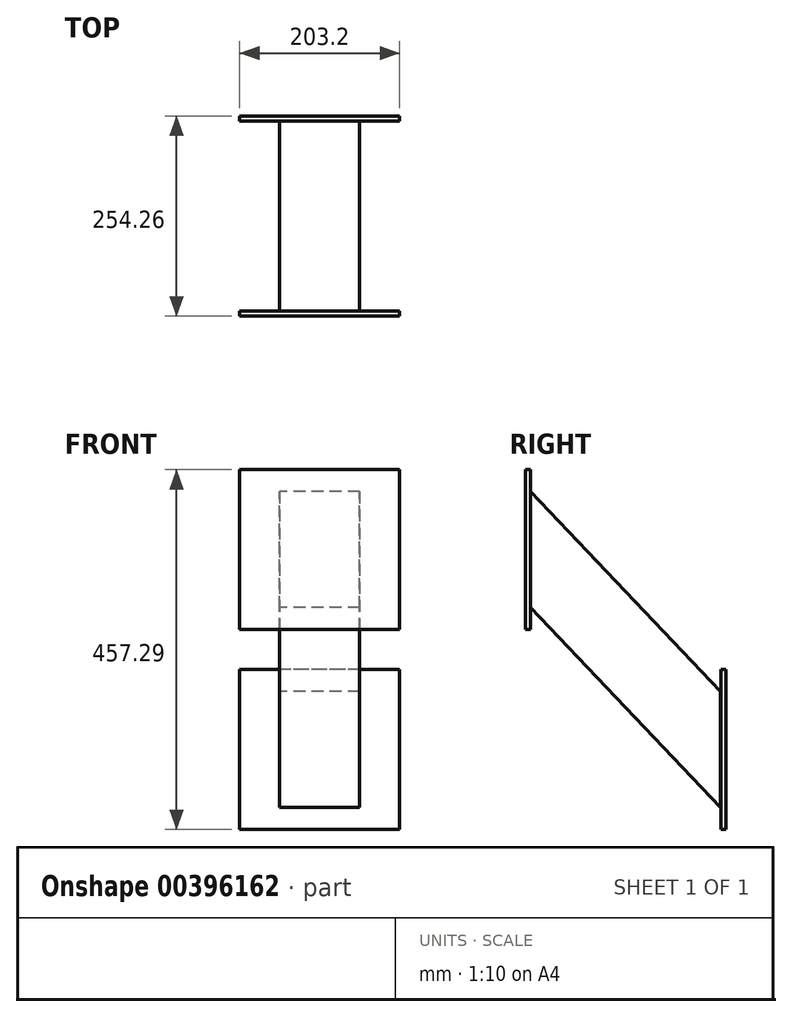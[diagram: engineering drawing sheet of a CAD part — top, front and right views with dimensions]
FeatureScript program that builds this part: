
annotation { "Feature Type Name" : "Feature", "Feature Type Description" : "" }
export const myFeature = defineFeature(function(context is Context, id is Id, definition is map)
    precondition{}
    {
        {
            var Q0;
            Q0=qCreatedBy(makeId("Right.planeOp"),FACE);
            var sketch = newSketch(context, id + "F0", { "sketchPlane" : qUnion([Q0])});
            skLineSegment(sketch, "E0.bottom", {"start": v(-67, -16.54) * mm, "end": v(-73.36, -16.54) * mm});
            skLineSegment(sketch, "E0.top", {"start": v(-67, 186.66) * mm, "end": v(-73.36, 186.66) * mm});
            skLineSegment(sketch, "E0.left", {"start": v(-67, -16.54) * mm, "end": v(-67, 186.66) * mm});
            skLineSegment(sketch, "E0.right", {"start": v(-73.36, -16.54) * mm, "end": v(-73.36, 186.66) * mm});
            skPoint(sketch, "E0.middle", {"position": v(-70.18, 85.06) * mm});
            skLineSegment(sketch, "E1", {"start": v(-67, 158.75) * mm, "end": v(174.3, -95.25) * mm});
            skLineSegment(sketch, "E2", {"start": v(174.3, -95.25) * mm, "end": v(174.3, -242.77) * mm});
            skLineSegment(sketch, "E3", {"start": v(174.3, -242.77) * mm, "end": v(-67, 11.23) * mm});
            skLineSegment(sketch, "E4", {"start": v(-67, 11.23) * mm, "end": v(-67, 158.75) * mm});
            skLineSegment(sketch, "E5.bottom", {"start": v(174.55, -67.39) * mm, "end": v(180.9, -67.39) * mm});
            skLineSegment(sketch, "E5.top", {"start": v(174.55, -270.63) * mm, "end": v(180.9, -270.63) * mm});
            skLineSegment(sketch, "E5.left", {"start": v(174.55, -67.39) * mm, "end": v(174.55, -270.63) * mm});
            skLineSegment(sketch, "E5.right", {"start": v(180.9, -67.39) * mm, "end": v(180.9, -270.63) * mm});
            skSolve(sketch);
        }
        {
            var Q0;
            {var subQ3=sQuery(id+"F0.wireOp",EDGE,"E0.bottom");Q0=makeQuery(id+"F0.imprint","IMPRINT",FACE,{"disambiguationData":[TD([[makeQuery(id+"F0.imprint","IMPRINT",EDGE,{"derivedFrom":subQ3}),-1.0]])]});}
            extrude(context, id + "F1", {"entities" : qUnion([Q0]), "depth" : 101.6 * mm, "hasSecondDirection" : true, "secondDirectionOppositeDirection" : true, "secondDirectionDepth" : 101.6 * mm});
        }
        {
            var Q0;
            Q0=makeQuery(id+"F0.imprint","IMPRINT",FACE,{"disambiguationData":[TD([[makeQuery(id+"F0.imprint","IMPRINT",EDGE,{"derivedFrom":sQuery(id+"F0.wireOp",EDGE,"E1")}),-1.0]])]});
            extrude(context, id + "F2", {"entities" : qUnion([Q0]), "operationType" : NewBodyOperationType.ADD, "depth" : 50.8 * mm, "hasSecondDirection" : true, "secondDirectionOppositeDirection" : true, "secondDirectionDepth" : 50.8 * mm});
        }
        {
            var Q0;
            Q0=makeQuery(id+"F0.imprint","IMPRINT",FACE,{"disambiguationData":[TD([[makeQuery(id+"F0.imprint","IMPRINT",EDGE,{"derivedFrom":sQuery(id+"F0.wireOp",EDGE,"E5.bottom")}),-1.0]])]});
            extrude(context, id + "F3", {"entities" : qUnion([Q0]), "depth" : 101.6 * mm, "hasSecondDirection" : true, "secondDirectionOppositeDirection" : true, "secondDirectionDepth" : 101.6 * mm});
        }
    });
